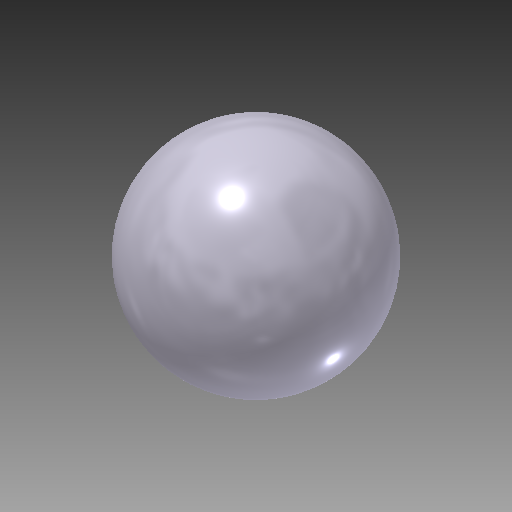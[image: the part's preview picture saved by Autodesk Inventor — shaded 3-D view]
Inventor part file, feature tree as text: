
AUTODESK INVENTOR PART (.ipt)
format: ipt  version: 2017 (Build 210142000, 142)  size: 146,944 bytes
history: native  units: mm (DEFAULTED — no unit token found)
features: revolve x2, sketch x2
ambient origin geometry x8: Origin, YZ Plane, XZ Plane, XY Plane, X Axis, Y Axis, Z Axis, Center Point
bodies: Solid1 (feature_tree)
feature tree (4):
  revolve  "Revolution1"  Angle=90.0deg
  revolve  "Revolution2"  Angle=90.0deg
  sketch  "Sketch1"  dims[d0=2.0mm d1=90.0deg]
  sketch  "Sketch2"  dims[d2=2.0mm d3=90.0deg]
